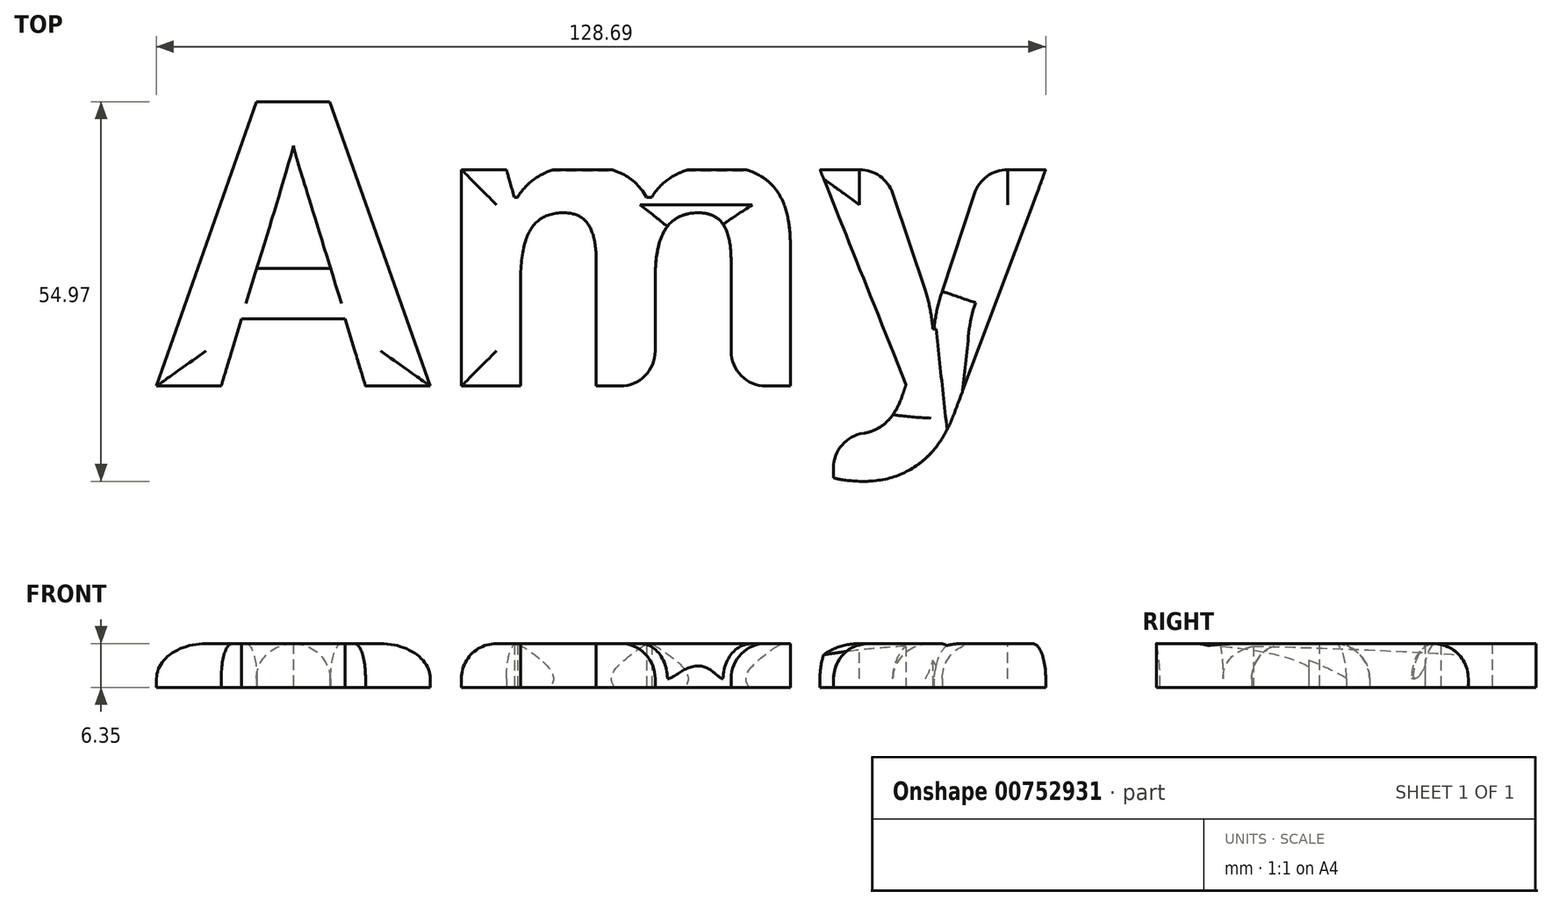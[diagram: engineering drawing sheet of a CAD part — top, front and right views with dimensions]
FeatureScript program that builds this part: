
annotation { "Feature Type Name" : "Feature", "Feature Type Description" : "" }
export const myFeature = defineFeature(function(context is Context, id is Id, definition is map)
    precondition{}
    {
        {
            var Q0;
            Q0=qCreatedBy(makeId("Top.planeOp"),FACE);
            var sketch = newSketch(context, id + "F0", { "sketchPlane" : qUnion([Q0])});
            skText(sketch, "E0", { "text": "Amy", "fontName": "OpenSans-Bold.ttf"});
            const initialGuessF0  = {"E0": [-0.07569, -0.04135, 1, 0, 0.04135]};
            skSetInitialGuess(sketch, initialGuessF0);
            skSolve(sketch);
        }
        {
            var Q0;
            Q0 = qSketchRegion(id + "F0", true);
            extrude(context, id + "F1", {"entities" : qUnion([Q0]), "depth" : 6.35 * mm, "offsetDistance" : 25.4 * mm});
        }
        {
            var Q0;
            Q0=makeQuery(id+"F1.opExtrude","CAP_EDGE",EDGE,{"disambiguationData":[OSD([sQuery(id+"F0.wireOp",EDGE,"E0.sketch_text.stroke-11")])],"isStart":false});
            fillet(context, id + "F2", {"entities" : qUnion([Q0]), "radius" : 5.08 * mm, "tangentPropagation" : true, "allowEdgeOverflow" : false});
        }
        {
            var Q0;
            Q0=makeQuery(id+"F1.opExtrude","CAP_EDGE",EDGE,{"disambiguationData":[OSD([sQuery(id+"F0.wireOp",EDGE,"E0.sketch_text.stroke-7")])],"isStart":false});
            var Q1;
            Q1=makeQuery(id+"F1.opExtrude","CAP_EDGE",EDGE,{"disambiguationData":[OSD([sQuery(id+"F0.wireOp",EDGE,"E0.sketch_text.stroke-3")])],"isStart":false});
            var Q2;
            Q2=makeQuery(id+"F1.opExtrude","CAP_EDGE",EDGE,{"disambiguationData":[OSD([sQuery(id+"F0.wireOp",EDGE,"E0.sketch_text.stroke-4")])],"isStart":false});
            var Q3;
            Q3=makeQuery(id+"F1.opExtrude","CAP_EDGE",EDGE,{"disambiguationData":[OSD([sQuery(id+"F0.wireOp",EDGE,"E0.sketch_text.stroke-6")])],"isStart":false});
            fillet(context, id + "F3", {"entities" : qUnion([Q0, Q1, Q2, Q3]), "radius" : 5.08 * mm, "tangentPropagation" : true, "allowEdgeOverflow" : false});
        }
        {
            var Q0;
            Q0=makeQuery(id+"F1.opExtrude","CAP_EDGE",EDGE,{"disambiguationData":[OSD([sQuery(id+"F0.wireOp",EDGE,"E0.sketch_text.stroke-21")])],"isStart":false});
            var Q1;
            Q1=makeQuery(id+"F1.opExtrude","CAP_EDGE",EDGE,{"disambiguationData":[OSD([sQuery(id+"F0.wireOp",EDGE,"E0.sketch_text.stroke-33")])],"isStart":false});
            var Q2;
            Q2=makeQuery(id+"F1.opExtrude","CAP_EDGE",EDGE,{"disambiguationData":[OSD([sQuery(id+"F0.wireOp",EDGE,"E0.sketch_text.stroke-19")])],"isStart":false});
            var Q3;
            Q3=makeQuery(id+"F1.opExtrude","CAP_EDGE",EDGE,{"disambiguationData":[OSD([sQuery(id+"F0.wireOp",EDGE,"E0.sketch_text.stroke-12")])],"isStart":false});
            var Q4;
            Q4=makeQuery(id+"F1.opExtrude","CAP_EDGE",EDGE,{"disambiguationData":[OSD([sQuery(id+"F0.wireOp",EDGE,"E0.sketch_text.stroke-20")])],"isStart":false});
            fillet(context, id + "F4", {"entities" : qUnion([Q0, Q1, Q2, Q3, Q4]), "radius" : 5.08 * mm, "tangentPropagation" : true, "allowEdgeOverflow" : false});
        }
        {
            var Q0;
            Q0=makeQuery(id+"F1.opExtrude","CAP_EDGE",EDGE,{"disambiguationData":[OSD([sQuery(id+"F0.wireOp",EDGE,"E0.sketch_text.stroke-34")])],"isStart":false});
            fillet(context, id + "F5", {"entities" : qUnion([Q0]), "radius" : 5.08 * mm, "tangentPropagation" : true, "allowEdgeOverflow" : false});
        }
        {
            var Q0;
            Q0=makeQuery(id+"F1.opExtrude","CAP_EDGE",EDGE,{"disambiguationData":[OSD([sQuery(id+"F0.wireOp",EDGE,"E0.sketch_text.stroke-40")])],"isStart":false});
            var Q1;
            Q1=makeQuery(id+"F1.opExtrude","CAP_EDGE",EDGE,{"disambiguationData":[OSD([sQuery(id+"F0.wireOp",EDGE,"E0.sketch_text.stroke-46")])],"isStart":false});
            var Q2;
            Q2=makeQuery(id+"F1.opExtrude","CAP_EDGE",EDGE,{"disambiguationData":[OSD([sQuery(id+"F0.wireOp",EDGE,"E0.sketch_text.stroke-51")])],"isStart":false});
            fillet(context, id + "F6", {"entities" : qUnion([Q0, Q1, Q2]), "radius" : 5.08 * mm, "tangentPropagation" : true, "allowEdgeOverflow" : false});
        }
        {
            var Q0;
            Q0=makeQuery(id+"F1.opExtrude","CAP_EDGE",EDGE,{"disambiguationData":[OSD([sQuery(id+"F0.wireOp",EDGE,"E0.sketch_text.stroke-41")])],"isStart":false});
            fillet(context, id + "F7", {"entities" : qUnion([Q0]), "radius" : 5.08 * mm, "tangentPropagation" : true, "allowEdgeOverflow" : false});
        }
        {
            var Q0;
            Q0=makeQuery(id+"F1.opExtrude","CAP_EDGE",EDGE,{"disambiguationData":[OSD([sQuery(id+"F0.wireOp",EDGE,"E0.sketch_text.stroke-45")])],"isStart":false});
            fillet(context, id + "F8", {"entities" : qUnion([Q0]), "radius" : 5.08 * mm, "tangentPropagation" : true, "allowEdgeOverflow" : false});
        }
        {
            var Q0;
            Q0=makeQuery(id+"F1.opExtrude","CAP_EDGE",EDGE,{"disambiguationData":[OSD([sQuery(id+"F0.wireOp",EDGE,"E0.sketch_text.stroke-54")])],"isStart":false});
            fillet(context, id + "F9", {"entities" : qUnion([Q0]), "radius" : 5.08 * mm, "tangentPropagation" : true, "allowEdgeOverflow" : false});
        }
    });
